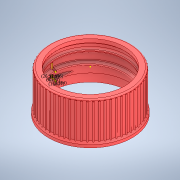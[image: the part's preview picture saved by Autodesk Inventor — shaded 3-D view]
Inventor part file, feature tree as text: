
AUTODESK INVENTOR PART (.ipt)
format: ipt  version: 2022.1 (Build 261234020, 234B)  size: 1,184,768 bytes
history: mixed  units: in
note: dims shown in document units (in); Inventor stores cm internally (conversion verified against a paired STEP export)
features: sketch x2, extrude x1, other x1, imported_body x1
ambient origin geometry x8: Origin, YZ Plane, XZ Plane, XY Plane, X Axis, Y Axis, Z Axis, Center Point
bodies: Solid1 (imported_parasolid)
feature tree (5):
  sketch  "Sketch1"  dims[d0=0.1827in d1=0.0591in]
  extrude  "Extrusion1"  Depth=0.0591in
  sketch  "Sketch2"  dims[d3=0.0549in d4=0.0098in d5=0.0076in d6=0.0492in d7=0.1175in d8=0.9843in d9=0.0in d10=0.0in]
  other  "RipetizioneCircolare3"
  imported_body  NMx_Import_Brep_tag  [imported B-rep: ~5 faces, bbox_mm=None]
